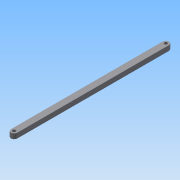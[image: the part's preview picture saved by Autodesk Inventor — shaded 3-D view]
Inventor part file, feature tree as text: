
AUTODESK INVENTOR PART (.ipt)
format: ipt  version: 2015 (Build 190159000, 159)  size: 74,752 bytes
history: native  units: mm
features: other x1, extrude x1, sketch x1
ambient origin geometry x8: Origin, YZ Plane, XZ Plane, XY Plane, X Axis, Y Axis, Z Axis, Center Point
bodies: Body1 (feature_tree)
feature tree (3):
  other  "實體1"
  extrude  "擠出1"  Depth=60.67mm
  sketch  "草圖1"
